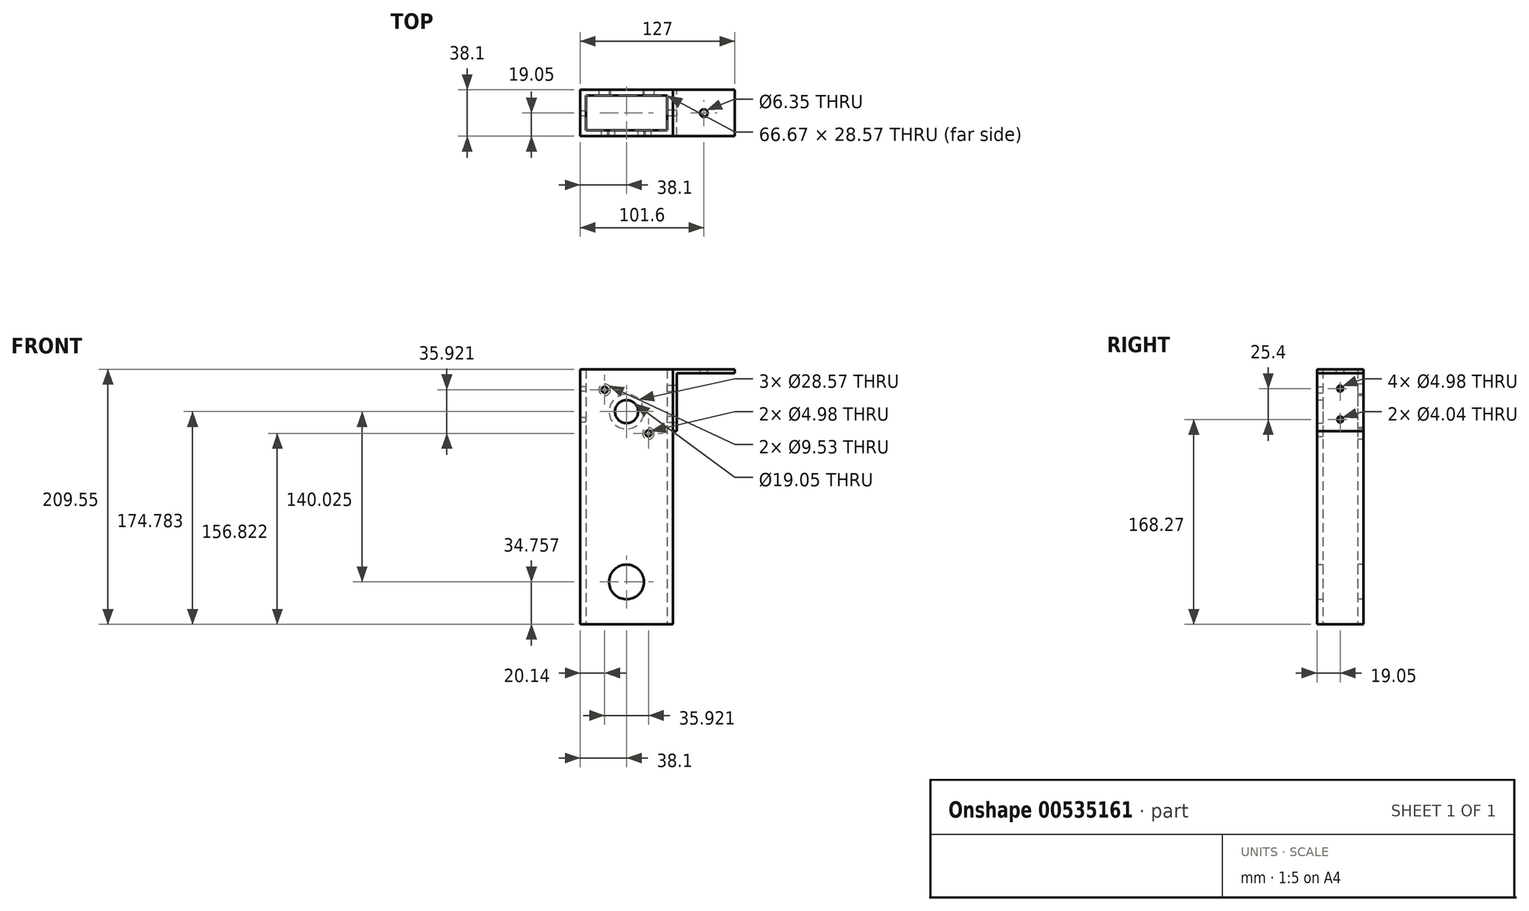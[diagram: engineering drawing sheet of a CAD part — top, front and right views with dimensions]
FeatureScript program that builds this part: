
annotation { "Feature Type Name" : "Feature", "Feature Type Description" : "" }
export const myFeature = defineFeature(function(context is Context, id is Id, definition is map)
    precondition{}
    {
        {
            var Q0;
            Q0=qCreatedBy(makeId("Top.planeOp"),FACE);
            var sketch = newSketch(context, id + "F0", { "sketchPlane" : qUnion([Q0])});
            skLineSegment(sketch, "E0.bottom", {"start": v(-38.1, 19.05) * mm, "end": v(38.1, 19.05) * mm});
            skLineSegment(sketch, "E0.top", {"start": v(-38.1, -19.05) * mm, "end": v(38.1, -19.05) * mm});
            skLineSegment(sketch, "E0.left", {"start": v(-38.1, 19.05) * mm, "end": v(-38.1, -19.05) * mm});
            skLineSegment(sketch, "E0.right", {"start": v(38.1, 19.05) * mm, "end": v(38.1, -19.05) * mm});
            skSolve(sketch);
        }
        {
            var Q0;
            Q0=makeQuery(id+"F0.imprint","IMPRINT",FACE,{"disambiguationData":[TD([[makeQuery(id+"F0.imprint","IMPRINT",EDGE,{"derivedFrom":sQuery(id+"F0.wireOp",EDGE,"E0.bottom")}),-1.0]])]});
            extrude(context, id + "F1", {"entities" : qUnion([Q0]), "endBound" : BoundingType.SYMMETRIC, "depth" : 209.55 * mm});
        }
        {
            var Q0;
            Q0=makeQuery(id+"F1.opExtrude","CAP_FACE",FACE,{"disambiguationData":[OSD([sQuery(id+"F0.wireOp",EDGE,"E0.bottom"),sQuery(id+"F0.wireOp",EDGE,"E0.top"),sQuery(id+"F0.wireOp",EDGE,"E0.left"),sQuery(id+"F0.wireOp",EDGE,"E0.right")])],"isStart":false});
            var Q1;
            Q1=makeQuery(id+"F1.opExtrude","CAP_FACE",FACE,{"disambiguationData":[OSD([sQuery(id+"F0.wireOp",EDGE,"E0.bottom"),sQuery(id+"F0.wireOp",EDGE,"E0.top"),sQuery(id+"F0.wireOp",EDGE,"E0.left"),sQuery(id+"F0.wireOp",EDGE,"E0.right")])],"isStart":true});
            shell(context, id + "F2", {"entities" : qUnion([Q0, Q1]), "thickness" : 4.76 * mm});
        }
        {
            var Q0;
            Q0=qCreatedBy(makeId("Front.planeOp"),FACE);
            var sketch = newSketch(context, id + "F3", { "sketchPlane" : qUnion([Q0])});
            skCircle(sketch, "E1", {"center": v(0, 70.01) * mm, "radius": 9.53 * mm});
            skCircle(sketch, "E2", {"center": v(0, -70.01) * mm, "radius": 14.29 * mm});
            skCircle(sketch, "E3", {"center": v(0, 70.01) * mm, "radius": 14.29 * mm});
            skCircle(sketch, "E4", {"center": v(-17.96, 87.97) * mm, "radius": 2.49 * mm});
            skCircle(sketch, "E5", {"center": v(17.96, 52.05) * mm, "radius": 2.49 * mm});
            skCircle(sketch, "E6", {"center": v(-17.96, 87.97) * mm, "radius": 4.76 * mm});
            skCircle(sketch, "E7", {"center": v(17.96, 52.05) * mm, "radius": 4.76 * mm});
            skCircle(sketch, "E8", {"center": v(0, 70.01) * mm, "radius": 25.4 * mm, "construction": true});
            skLineSegment(sketch, "E9", {"start": v(-17.96, 87.97) * mm, "end": v(17.96, 52.05) * mm, "construction": true});
            skSolve(sketch);
        }
        {
            var Q0;
            Q0=makeQuery(id+"F3.imprint","IMPRINT",FACE,{"disambiguationData":[TD([[makeQuery(id+"F3.imprint","IMPRINT",EDGE,{"derivedFrom":sQuery(id+"F3.wireOp",EDGE,"E1")}),1.0]])]});
            var Q1;
            Q1=makeQuery(id+"F3.imprint","IMPRINT",FACE,{"disambiguationData":[TD([[makeQuery(id+"F3.imprint","IMPRINT",EDGE,{"derivedFrom":sQuery(id+"F3.wireOp",EDGE,"E4")}),1.0]])]});
            var Q2;
            Q2=makeQuery(id+"F3.imprint","IMPRINT",FACE,{"disambiguationData":[TD([[makeQuery(id+"F3.imprint","IMPRINT",EDGE,{"derivedFrom":sQuery(id+"F3.wireOp",EDGE,"E5")}),1.0]])]});
            var Q3;
            Q3=makeQuery(id+"F3.imprint","IMPRINT",FACE,{"disambiguationData":[TD([[makeQuery(id+"F3.imprint","IMPRINT",EDGE,{"derivedFrom":sQuery(id+"F3.wireOp",EDGE,"E2")}),1.0]])]});
            extrude(context, id + "F4", {"entities" : qUnion([Q0, Q1, Q2, Q3]), "operationType" : NewBodyOperationType.REMOVE, "endBound" : BoundingType.THROUGH_ALL, "depth" : 25.4 * mm});
        }
        {
            var Q0;
            Q0=makeQuery(id+"F3.imprint","IMPRINT",FACE,{"disambiguationData":[TD([[makeQuery(id+"F3.imprint","IMPRINT",EDGE,{"derivedFrom":sQuery(id+"F3.wireOp",EDGE,"E4")}),-1.0]])]});
            var Q1;
            Q1=makeQuery(id+"F3.imprint","IMPRINT",FACE,{"disambiguationData":[TD([[makeQuery(id+"F3.imprint","IMPRINT",EDGE,{"derivedFrom":sQuery(id+"F3.wireOp",EDGE,"E4")}),1.0]])]});
            var Q2;
            Q2=makeQuery(id+"F3.imprint","IMPRINT",FACE,{"disambiguationData":[TD([[makeQuery(id+"F3.imprint","IMPRINT",EDGE,{"derivedFrom":sQuery(id+"F3.wireOp",EDGE,"E1")}),1.0]])]});
            var Q3;
            Q3=makeQuery(id+"F3.imprint","IMPRINT",FACE,{"disambiguationData":[TD([[makeQuery(id+"F3.imprint","IMPRINT",EDGE,{"derivedFrom":sQuery(id+"F3.wireOp",EDGE,"E1")}),-1.0]])]});
            var Q4;
            Q4=makeQuery(id+"F3.imprint","IMPRINT",FACE,{"disambiguationData":[TD([[makeQuery(id+"F3.imprint","IMPRINT",EDGE,{"derivedFrom":sQuery(id+"F3.wireOp",EDGE,"E5")}),1.0]])]});
            var Q5;
            Q5=makeQuery(id+"F3.imprint","IMPRINT",FACE,{"disambiguationData":[TD([[makeQuery(id+"F3.imprint","IMPRINT",EDGE,{"derivedFrom":sQuery(id+"F3.wireOp",EDGE,"E5")}),-1.0]])]});
            var Q6;
            Q6=makeQuery(id+"F3.imprint","IMPRINT",FACE,{"disambiguationData":[TD([[makeQuery(id+"F3.imprint","IMPRINT",EDGE,{"derivedFrom":sQuery(id+"F3.wireOp",EDGE,"E2")}),1.0]])]});
            extrude(context, id + "F5", {"entities" : qUnion([Q0, Q1, Q2, Q3, Q4, Q5, Q6]), "operationType" : NewBodyOperationType.REMOVE, "oppositeDirection" : true, "depth" : 25.4 * mm});
        }
        {
            var Q0;
            Q0=qCreatedBy(makeId("Front.planeOp"),FACE);
            var sketch = newSketch(context, id + "F6", { "sketchPlane" : qUnion([Q0])});
            skLineSegment(sketch, "E10", {"start": v(38.1, 53.98) * mm, "end": v(38.1, 104.78) * mm});
            skLineSegment(sketch, "E11", {"start": v(38.1, 104.78) * mm, "end": v(88.9, 104.78) * mm});
            skLineSegment(sketch, "E12", {"start": v(88.9, 104.78) * mm, "end": v(88.9, 101.6) * mm});
            skLineSegment(sketch, "E13", {"start": v(88.9, 101.6) * mm, "end": v(41.28, 101.6) * mm});
            skLineSegment(sketch, "E14", {"start": v(41.28, 101.6) * mm, "end": v(41.28, 53.98) * mm});
            skLineSegment(sketch, "E15", {"start": v(41.28, 53.98) * mm, "end": v(38.1, 53.98) * mm});
            skSolve(sketch);
        }
        {
            var Q0;
            Q0=makeQuery(id+"F6.imprint","IMPRINT",FACE,{"disambiguationData":[TD([[makeQuery(id+"F6.imprint","IMPRINT",EDGE,{"derivedFrom":sQuery(id+"F6.wireOp",EDGE,"E10")}),-1.0]])]});
            extrude(context, id + "F7", {"entities" : qUnion([Q0]), "endBound" : BoundingType.SYMMETRIC, "depth" : 38.1 * mm});
        }
        {
            var Q0;
            Q0=qCreatedBy(makeId("Right.planeOp"),FACE);
            var sketch = newSketch(context, id + "F8", { "sketchPlane" : qUnion([Q0])});
            skCircle(sketch, "E16", {"center": v(0, 88.9) * mm, "radius": 2.02 * mm});
            skCircle(sketch, "E17", {"center": v(0, 63.5) * mm, "radius": 2.02 * mm});
            skCircle(sketch, "E18", {"center": v(0, 88.9) * mm, "radius": 2.49 * mm});
            skCircle(sketch, "E19", {"center": v(0, 63.5) * mm, "radius": 2.49 * mm});
            skSolve(sketch);
        }
        {
            var Q0;
            Q0=makeQuery(id+"F8.imprint","IMPRINT",FACE,{"disambiguationData":[TD([[makeQuery(id+"F8.imprint","IMPRINT",EDGE,{"derivedFrom":sQuery(id+"F8.wireOp",EDGE,"E16")}),1.0]])]});
            var Q1;
            Q1=makeQuery(id+"F8.imprint","IMPRINT",FACE,{"disambiguationData":[TD([[makeQuery(id+"F8.imprint","IMPRINT",EDGE,{"derivedFrom":sQuery(id+"F8.wireOp",EDGE,"E17")}),1.0]])]});
            extrude(context, id + "F9", {"entities" : qUnion([Q0, Q1]), "operationType" : NewBodyOperationType.REMOVE, "endBound" : BoundingType.THROUGH_ALL, "oppositeDirection" : true, "depth" : 25.4 * mm, "hasSecondDirection" : true, "secondDirectionBound" : SecondDirectionBoundingType.THROUGH_ALL, "secondDirectionOppositeDirection" : false, "secondDirectionDepth" : 25.4 * mm});
        }
        {
            var Q0;
            Q0=makeQuery(id+"F7.opExtrude","SWEPT_FACE",FACE,{"disambiguationData":[OSD([sQuery(id+"F6.wireOp",EDGE,"E11")])]});
            var sketch = newSketch(context, id + "F10", { "sketchPlane" : qUnion([Q0])});
            skCircle(sketch, "E20", {"center": v(63.5, 0) * mm, "radius": 3.18 * mm});
            skPoint(sketch, "E20.centerSnap0", {"position": v(63.5, -19.05) * mm});
            skPoint(sketch, "E20.centerSnap1", {"position": v(88.9, 0) * mm});
            skSolve(sketch);
        }
        {
            var Q0;
            Q0=makeQuery(id+"F10.imprint","IMPRINT",FACE,{"disambiguationData":[TD([[makeQuery(id+"F10.imprint","IMPRINT",EDGE,{"derivedFrom":sQuery(id+"F10.wireOp",EDGE,"E20")}),1.0]])]});
            extrude(context, id + "F11", {"entities" : qUnion([Q0]), "operationType" : NewBodyOperationType.REMOVE, "endBound" : BoundingType.THROUGH_ALL, "oppositeDirection" : true, "depth" : 25.4 * mm});
        }
        {
            var Q0;
            Q0=makeQuery(id+"F8.imprint","IMPRINT",FACE,{"disambiguationData":[TD([[makeQuery(id+"F8.imprint","IMPRINT",EDGE,{"derivedFrom":sQuery(id+"F8.wireOp",EDGE,"E16")}),1.0]])]});
            var Q1;
            Q1=makeQuery(id+"F8.imprint","IMPRINT",FACE,{"disambiguationData":[TD([[makeQuery(id+"F8.imprint","IMPRINT",EDGE,{"derivedFrom":sQuery(id+"F8.wireOp",EDGE,"E16")}),-1.0]])]});
            var Q2;
            Q2=makeQuery(id+"F8.imprint","IMPRINT",FACE,{"disambiguationData":[TD([[makeQuery(id+"F8.imprint","IMPRINT",EDGE,{"derivedFrom":sQuery(id+"F8.wireOp",EDGE,"E17")}),1.0]])]});
            var Q3;
            Q3=makeQuery(id+"F8.imprint","IMPRINT",FACE,{"disambiguationData":[TD([[makeQuery(id+"F8.imprint","IMPRINT",EDGE,{"derivedFrom":sQuery(id+"F8.wireOp",EDGE,"E17")}),-1.0]])]});
            extrude(context, id + "F12", {"entities" : qUnion([Q0, Q1, Q2, Q3]), "operationType" : NewBodyOperationType.REMOVE, "endBound" : BoundingType.THROUGH_ALL, "depth" : 25.4 * mm});
        }
    });
